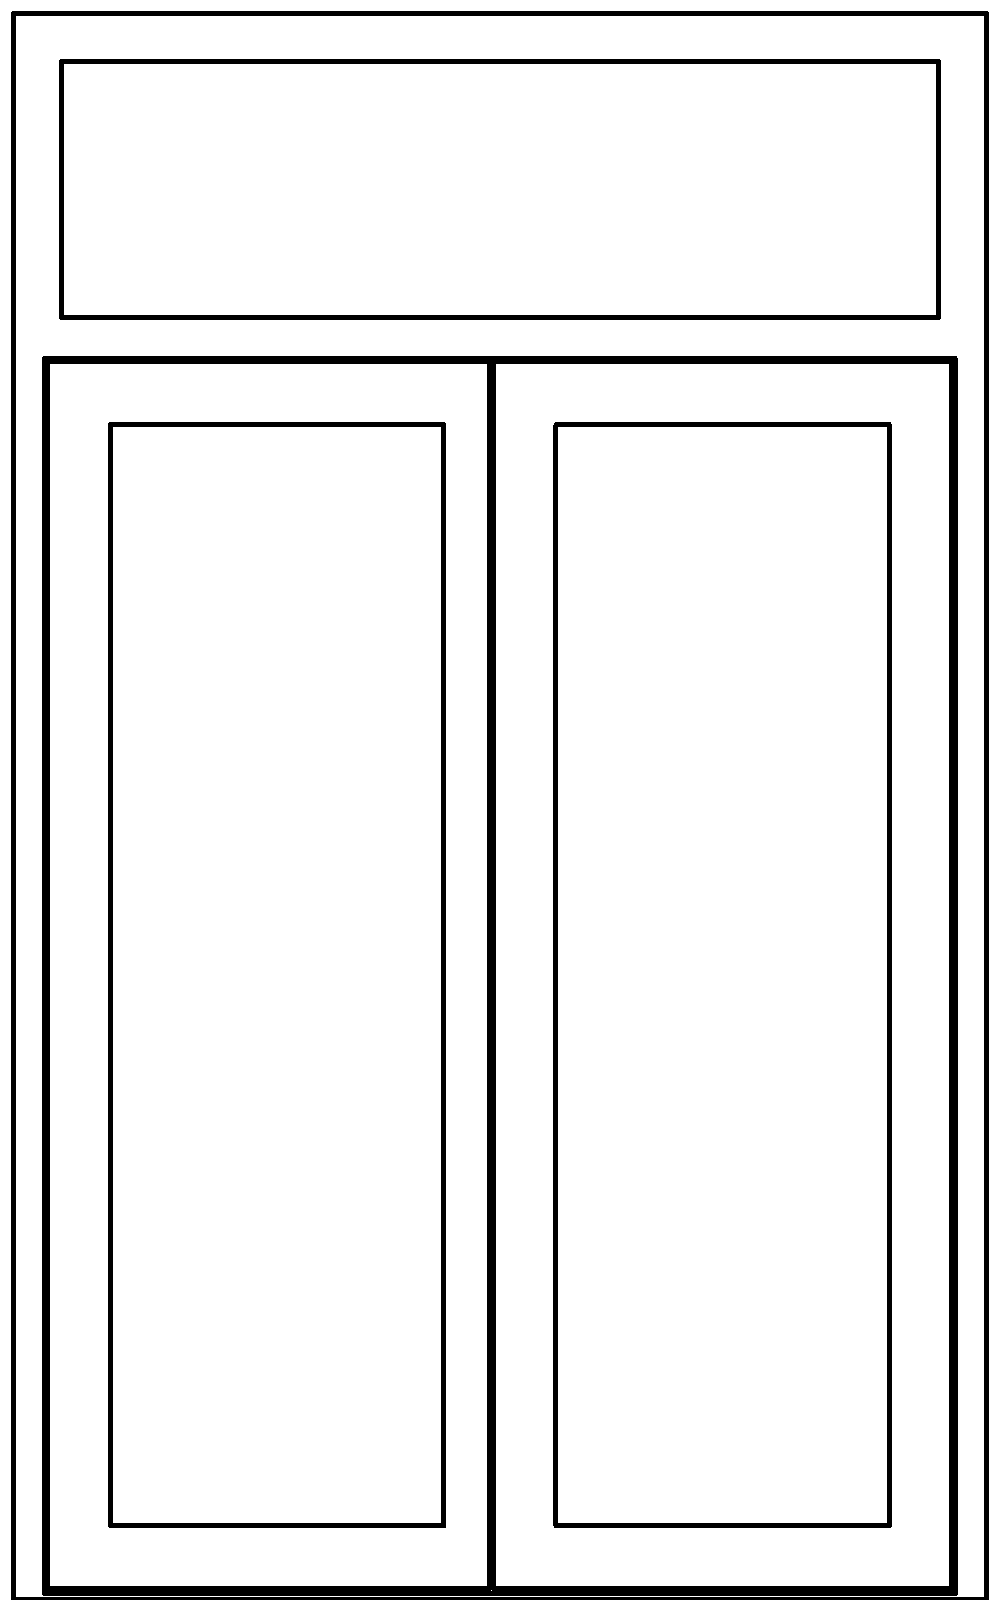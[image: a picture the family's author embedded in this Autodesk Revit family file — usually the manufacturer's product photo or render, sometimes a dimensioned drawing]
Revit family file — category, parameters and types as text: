
# Revit family: Дверь.Alumark_двупольная с глухим окном_S44
name_source: partatom
category: Двери
revit_build: Autodesk Revit 2017 (Build: 20171027_0315(x64)
units: mm (PartAtom-declared; Revit-internal decimal feet)

## family parameters
Всегда вертикально = Да
Заголовок OmniClass = Doors
Номер OmniClass = 23.30.10.00
Общий = Нет
Основа = Стена
При загрузке вырезать с полостями = Нет
Точка расчета площади = Нет

## types (2) — shared parameters
ADSK_Завод-изготовитель = ТБМ
ADSK_Обозначение = ГОСТ 23747-2015
URL = http://www.tbm.ru
sp_energy = Энергосберегающие стекла
sp_gaz = Заполненный газом
sp_standart = Обычный стеклопакет
Аналитическая конструкция = Застеклённая створчатая дверь, металлическая рама с двумя стеклами
Высота импоста = 800 мм
Дверь с цоколем = Нет
Заполнение стеклопакета = Обычный стеклопакет
Изготовитель = ТБМ
Изображение типоразмера = схема_двупольная_дверь_фрамуга.png
Импост двери = Нет
Коэффициент теплопередачи (U) = 4.2812 Вт/(м²·K)
Материал остекления = <По категории>
Материал профилей = <По категории>
Материал фурнитуры = <По категории>
Одинаковые полотна = Да
Окно высота = 300 мм
Описание = Дверь Проем ТБМ
Примерная высота = 2380 мм
Примерная ширина = 1160 мм
Разработчик = ООО ПРОРУБИМ
Разработчик (телефон) = +7(495)649-85-43
ТБМ_Артикул_Импост = ALM244301
ТБМ_Артикул_Крепление порога = ALM744630
ТБМ_Артикул_Подкладка под СП = ALM744307
ТБМ_Артикул_Порог = ALM244391
ТБМ_Артикул_Притвор = ALM244806
ТБМ_Артикул_Рама = ALM244100
ТБМ_Артикул_Распорный штифт = ALM885014
ТБМ_Артикул_Съемный ус = ALM244803
ТБМ_Артикул_Т-соединитель рамы = ALM744601
ТБМ_Артикул_Угловой соединитель рамы = ALM770421
ТБМ_Артикул_Уголок выравнивающий = ALM744014
ТБМ_Артикул_Уголок выравнивающий 2 = ALM744008
ТБМ_Артикул_Уплотнитель внутренний = ALM770207
ТБМ_Артикул_Уплотнитель наружный = ALM770004
ТБМ_Артикул_Уплотнитель порога = ELM0336
ТБМ_Артикул_Уплотнитель притвора = ALM770020
ТБМ_Артикул_Штапик = ALM244006
ТБМ_Длина_Импост = 1068 мм
ТБМ_Длина_Порог = 1068 мм
ТБМ_Длина_Притвор = 6296 мм
ТБМ_Длина_Рама = 5920 мм
ТБМ_Длина_Створка = 8244 мм
ТБМ_Длина_Створка 2 = 2048 мм
ТБМ_Длина_Съемный ус = 1508 мм
ТБМ_Длина_Уплотнитель внутренний = 6822 мм
ТБМ_Длина_Уплотнитель наружный = 6822 мм
ТБМ_Длина_Уплотнитель порога = 1068 мм
ТБМ_Длина_Уплотнитель притвора = 6296 мм
ТБМ_Длина_Штапик = 11878 мм
ТБМ_Количество_Крепление порога = 1
ТБМ_Количество_Подкладка под СП = 16
ТБМ_Количество_Распорный штифт = 20
ТБМ_Количество_Т-соединитель рамы = 2
ТБМ_Количество_Угловой соединитель рамы = 10
ТБМ_Количество_Уголок выравнивающий = 8
ТБМ_Количество_Уголок выравнивающий 2 = 8
ТБМ_Площадь стеклопакета = 1.76 м²
ТБМ_Стеклопакет_Высота 1 = 2172 мм
ТБМ_Стеклопакет_Высота 2 = 2172 мм
ТБМ_Стеклопакет_Ширина 1 = 405 мм
ТБМ_Стеклопакет_Ширина 2 = 405 мм
Термостойкость = 0.2336 (м²·K)/Вт
Тип стеклопакета = 24мм 1-камерный
Толщина = 44 мм
Функция = Наружные слои
Ширина створки слева = 460 мм
Ширина створки справа = 700 мм
автоматика = Фурнитура с автоматикой
импост_ширина = 62 мм
рама_ширина = 66 мм
сп_16_мм = 16мм 1-камерный
сп_24_мм = 24мм 1-камерный
створка_справа_ширина = 580 мм
створка_ширина = 84 мм
таблица выбора = каталог ТБМ двупольная дверь S44
фурнитура_высота = 2111 мм
штапик_толщина = 12 мм
zero-valued in all types: Коэффициент теплопритока от солнечного излучения, Пропускание видимого света, ТБМ_Длина_Притвор цоколя, ТБМ_Длина_Цоколь, ТБМ_Количество_Т-соединитель цоколя

## per-type parameters (varying)
| type | ADSK_Наименование | Открывание внутрь | Открывание наружу | ТБМ_Артикул_Створка | ТБМ_Артикул_Створка 2 | номер профиля |
| 1160х2380 Открывание наружу (СП 24мм Обычный) | ДАН О Оп Р (Однокамерный стеклопакет 24 мм) | Нет | Да | ALM244281 | ALM244280 | 11101 |
| 1160х2380 Открывание внутрь (СП 24мм Обычный) | ДАВ О Оп Р (Однокамерный стеклопакет 24 мм) | Да | Нет | ALM244280 | ALM244281 | 21101 |
